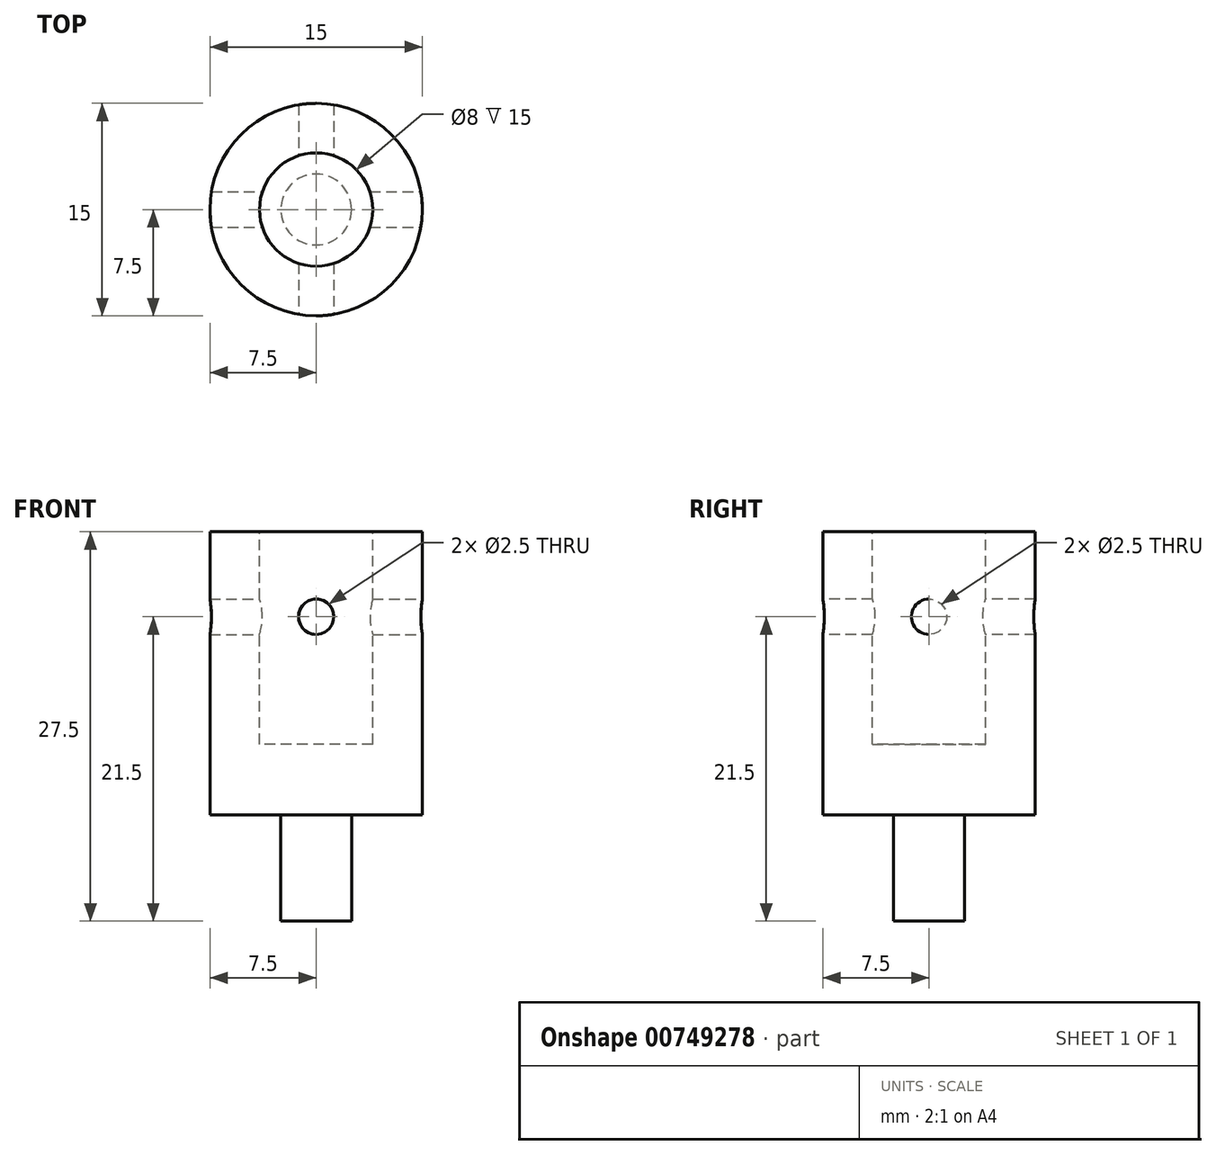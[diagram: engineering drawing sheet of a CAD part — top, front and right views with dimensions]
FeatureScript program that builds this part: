
annotation { "Feature Type Name" : "Feature", "Feature Type Description" : "" }
export const myFeature = defineFeature(function(context is Context, id is Id, definition is map)
    precondition{}
    {
        {
            var Q0;
            Q0=qCreatedBy(makeId("Top.planeOp"),FACE);
            var sketch = newSketch(context, id + "F0", { "sketchPlane" : qUnion([Q0])});
            skCircle(sketch, "E0", {"center": v(0, 0) * mm, "radius": 2.5 * mm});
            skSolve(sketch);
        }
        {
            var Q0;
            Q0 = qSketchRegion(id + "F0", true);
            extrude(context, id + "F1", {"entities" : qUnion([Q0]), "depth" : 7.5 * mm, "offsetDistance" : 25 * mm});
        }
        {
            var Q0;
            Q0=makeQuery(id+"F1.opExtrude","CAP_FACE",FACE,{"disambiguationData":[OSD([sQuery(id+"F0.wireOp",EDGE,"E0")])],"isStart":false});
            var sketch = newSketch(context, id + "F2", { "sketchPlane" : qUnion([Q0])});
            skCircle(sketch, "E1", {"center": v(0, 0) * mm, "radius": 7.5 * mm});
            skSolve(sketch);
        }
        {
            var Q0;
            Q0 = qSketchRegion(id + "F2", true);
            extrude(context, id + "F3", {"entities" : qUnion([Q0]), "operationType" : NewBodyOperationType.ADD, "depth" : 15 * mm, "offsetDistance" : 25 * mm});
        }
        {
            var Q0;
            Q0 = qSketchRegion(id + "F2", true);
            extrude(context, id + "F4", {"entities" : qUnion([Q0]), "operationType" : NewBodyOperationType.ADD, "depth" : 20 * mm, "offsetDistance" : 25 * mm});
        }
        {
            var Q0;
            Q0=makeQuery(id+"F4.opExtrude","CAP_FACE",FACE,{"disambiguationData":[OSD([sQuery(id+"F2.wireOp",EDGE,"E1")])],"isStart":false});
            var sketch = newSketch(context, id + "F5", { "sketchPlane" : qUnion([Q0])});
            skCircle(sketch, "E2", {"center": v(0, 0) * mm, "radius": 4 * mm});
            skSolve(sketch);
        }
        {
            var Q0;
            Q0 = qSketchRegion(id + "F5", true);
            extrude(context, id + "F6", {"entities" : qUnion([Q0]), "operationType" : NewBodyOperationType.REMOVE, "oppositeDirection" : true, "depth" : 15 * mm, "offsetDistance" : 25 * mm});
        }
        {
            var Q0;
            Q0=qCreatedBy(makeId("Front.planeOp"),FACE);
            var sketch = newSketch(context, id + "F7", { "sketchPlane" : qUnion([Q0])});
            skCircle(sketch, "E3", {"center": v(0, 21.5) * mm, "radius": 1.25 * mm});
            skSolve(sketch);
        }
        {
            var Q0;
            Q0 = qSketchRegion(id + "F7", true);
            extrude(context, id + "F8", {"entities" : qUnion([Q0]), "operationType" : NewBodyOperationType.REMOVE, "endBound" : BoundingType.THROUGH_ALL, "oppositeDirection" : true, "depth" : 25 * mm, "offsetDistance" : 25 * mm, "hasSecondDirection" : true, "secondDirectionBound" : SecondDirectionBoundingType.THROUGH_ALL, "secondDirectionOppositeDirection" : false, "secondDirectionDepth" : 25 * mm});
        }
        {
            var Q0;
            Q0=qCreatedBy(makeId("Right.planeOp"),FACE);
            var sketch = newSketch(context, id + "F9", { "sketchPlane" : qUnion([Q0])});
            skCircle(sketch, "E4", {"center": v(0, 21.5) * mm, "radius": 1.25 * mm});
            skSolve(sketch);
        }
        {
            var Q0;
            Q0 = qSketchRegion(id + "F9", true);
            extrude(context, id + "F10", {"entities" : qUnion([Q0]), "operationType" : NewBodyOperationType.REMOVE, "endBound" : BoundingType.THROUGH_ALL, "oppositeDirection" : true, "depth" : 25 * mm, "offsetDistance" : 25 * mm, "hasSecondDirection" : true, "secondDirectionBound" : SecondDirectionBoundingType.THROUGH_ALL, "secondDirectionOppositeDirection" : false, "secondDirectionDepth" : 25 * mm});
        }
    });
